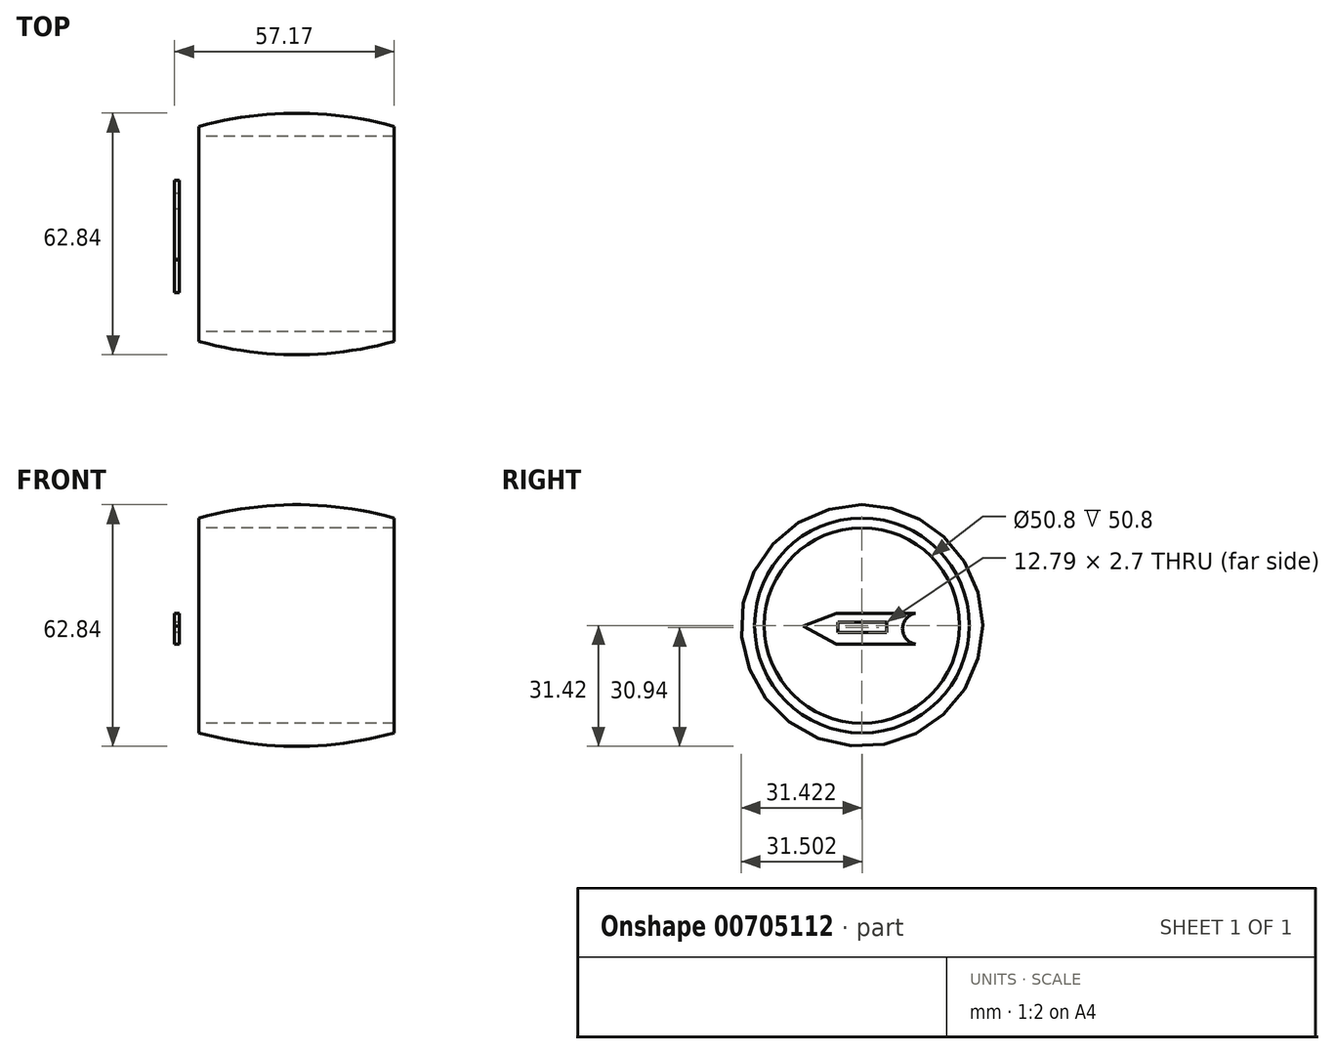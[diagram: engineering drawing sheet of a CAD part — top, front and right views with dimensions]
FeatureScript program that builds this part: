
annotation { "Feature Type Name" : "Feature", "Feature Type Description" : "" }
export const myFeature = defineFeature(function(context is Context, id is Id, definition is map)
    precondition{}
    {
        {
            var Q0;
            Q0=qCreatedBy(makeId("Right.planeOp"),FACE);
            var sketch = newSketch(context, id + "F0", { "sketchPlane" : qUnion([Q0])});
            skLineSegment(sketch, "E0", {"start": v(-101.6, -31.75) * mm, "end": v(153.5, -31.75) * mm, "construction": true});
            skCircle(sketch, "E1", {"center": v(-72.7, 0) * mm, "radius": 31.75 * mm});
            skCircle(sketch, "E2", {"center": v(130.5, -3.17) * mm, "radius": 28.58 * mm});
            skLineSegment(sketch, "E3", {"start": v(130.5, -3.18) * mm, "end": v(61.5, 57.58) * mm});
            skLineSegment(sketch, "E4", {"start": v(64.6, 54.85) * mm, "end": v(61.5, 51.33) * mm});
            skLineSegment(sketch, "E5", {"start": v(61.5, 51.33) * mm, "end": v(80.38, 34.69) * mm});
            skLineSegment(sketch, "E6", {"start": v(80.38, 34.69) * mm, "end": v(83.49, 38.21) * mm});
            skLineSegment(sketch, "E7", {"start": v(-72.7, 0) * mm, "end": v(65.82, 47.52) * mm});
            skLineSegment(sketch, "E8", {"start": v(-72.7, 0) * mm, "end": v(-14.9, -26.91) * mm});
            skLineSegment(sketch, "E9", {"start": v(-14.9, -26.91) * mm, "end": v(50.1, -26.91) * mm});
            skLineSegment(sketch, "E10", {"start": v(56.18, -22.36) * mm, "end": v(74.58, 39.8) * mm});
            skLineSegment(sketch, "E11", {"start": v(-14.9, -26.91) * mm, "end": v(-14.9, 19.83) * mm});
            skLineSegment(sketch, "E12", {"start": v(71.18, 28.32) * mm, "end": v(38.25, 38.06) * mm});
            skLineSegment(sketch, "E13", {"start": v(-58.83, 4.76) * mm, "end": v(-79.72, 4.76) * mm});
            skLineSegment(sketch, "E14", {"start": v(-58.83, -6.46) * mm, "end": v(-79.72, -6.46) * mm});
            skPoint(sketch, "E15.visualSharp", {"position": v(54.84, -26.91) * mm});
            skArc(sketch, "E15.filletArc", {"start": v(50.1, -26.91) * mm, "mid": v(53.9, -25.65) * mm, "end": v(56.18, -22.36) * mm});
            skCircle(sketch, "E16.0", {"center": v(-72.7, 0) * mm, "radius": 25.4 * mm});
            skCircle(sketch, "E17.0", {"center": v(130.5, -3.17) * mm, "radius": 22.23 * mm});
            skSolve(sketch);
        }
        {
            var Q0;
            Q0=qCreatedBy(makeId("Top.planeOp"),FACE);
            var Q1;
            Q1=sQuery(id+"F0.wireOp",VERTEX,"E8.start");
            cPlane(context, id + "F1", {"entities" : qUnion([Q0, Q1]), "cplaneType" : CPlaneType.PLANE_POINT, "offset" : 25.4 * mm, "width" : 152.4 * mm, "height" : 152.4 * mm});
        }
        {
            var Q0;
            Q0=qCreatedBy(id+"F1.planeOp",FACE);
            var sketch = newSketch(context, id + "F2", { "sketchPlane" : qUnion([Q0])});
            skLineSegment(sketch, "E18", {"start": v(0, -240.54) * mm, "end": v(0, 31.8) * mm, "construction": true});
            skLineSegment(sketch, "E19", {"start": v(-71.33, -156.1) * mm, "end": v(85.42, -156.1) * mm, "construction": true});
            skLineSegment(sketch, "E20", {"start": v(-25.4, -47.3) * mm, "end": v(25.4, -47.3) * mm});
            skPoint(sketch, "E21", {"position": v(0, -47.3) * mm});
            skLineSegment(sketch, "E22", {"start": v(25.4, -47.3) * mm, "end": v(25.4, -44.77) * mm});
            skLineSegment(sketch, "E23", {"start": v(-25.4, -47.3) * mm, "end": v(-25.4, -44.77) * mm});
            skArc(sketch, "E24", {"start": v(25.4, -44.77) * mm, "mid": v(0, -41.29) * mm, "end": v(-25.4, -44.77) * mm});
            skLineSegment(sketch, "E25", {"start": v(-23.52, -72.7) * mm, "end": v(23.66, -72.7) * mm, "construction": true});
            skSolve(sketch);
        }
        {
            var Q0;
            Q0=makeQuery(id+"F2.imprint","IMPRINT",FACE,{"disambiguationData":[TD([[makeQuery(id+"F2.imprint","IMPRINT",EDGE,{"derivedFrom":sQuery(id+"F2.wireOp",EDGE,"E20")}),1.0]])]});
            var Q1;
            Q1=sQuery(id+"F0.wireOp",EDGE,"E16.0");
            revolve(context, id + "F3", {"surfaceOperationType" : NewSurfaceOperationType.NEW, "entities" : qUnion([Q0]), "axis" : qUnion([Q1]), "revolveType" : RevolveType.FULL});
        }
        {
            var Q0;
            Q0=qCreatedBy(id+"F1.planeOp",FACE);
            var sketch = newSketch(context, id + "F4", { "sketchPlane" : qUnion([Q0])});
            skLineSegment(sketch, "E26", {"start": v(-28.81, -47.61) * mm, "end": v(-28.81, -41.26) * mm});
            skLineSegment(sketch, "E27", {"start": v(29.5, -47.42) * mm, "end": v(29.5, -41.07) * mm});
            skArc(sketch, "E28", {"start": v(29.5, -41.07) * mm, "mid": v(0.32, -36.16) * mm, "end": v(-28.81, -41.26) * mm});
            skSolve(sketch);
        }
        {
            var Q0;
            Q0=sQuery(id+"F4.wireOp",EDGE,"E26");
            var Q1;
            Q1=sQuery(id+"F4.wireOp",EDGE,"E28");
            var Q2;
            Q2=sQuery(id+"F4.wireOp",EDGE,"E27");
            var Q3;
            Q3=sQuery(id+"F0.wireOp",EDGE,"E16.0");
            revolve(context, id + "F5", {"bodyType" : ToolBodyType.SURFACE, "surfaceOperationType" : NewSurfaceOperationType.NEW, "surfaceEntities" : qUnion([Q0, Q1, Q2]), "axis" : qUnion([Q3]), "revolveType" : RevolveType.ONE_DIRECTION, "angle" : 130 * degree});
        }
        {
            var Q0;
            Q0=sQuery(id+"F0.wireOp",EDGE,"E7");
            cPlane(context, id + "F6", {"entities" : qUnion([Q0]), "cplaneType" : CPlaneType.LINE_ANGLE, "offset" : 25.4 * mm, "angle" : 0 * degree, "width" : 152.4 * mm, "height" : 152.4 * mm});
        }
        {
            var Q0;
            Q0=qCreatedBy(id+"F6.planeOp",FACE);
            var sketch = newSketch(context, id + "F7", { "sketchPlane" : qUnion([Q0])});
            skLineSegment(sketch, "E29", {"start": v(0, -0.48) * mm, "end": v(-31.13, -26.6) * mm});
            skLineSegment(sketch, "E30", {"start": v(0, -0.48) * mm, "end": v(31.13, -26.6) * mm});
            skLineSegment(sketch, "E31", {"start": v(-31.13, -26.6) * mm, "end": v(31.13, -26.6) * mm});
            skLineSegment(sketch, "E32", {"start": v(-30.35, -23.32) * mm, "end": v(32.35, -23.32) * mm});
            skSolve(sketch);
        }
        {
            var Q0;
            Q0=sQuery(id+"F7.wireOp",VERTEX,"E31.start");
            var Q1;
            Q1=sQuery(id+"F7.wireOp",EDGE,"E31");
            cPlane(context, id + "F8", {"entities" : qUnion([Q0, Q1]), "cplaneType" : CPlaneType.LINE_POINT, "offset" : 25.4 * mm, "width" : 152.4 * mm, "height" : 152.4 * mm});
        }
        {
            var Q0;
            Q0=qCreatedBy(id+"F8.planeOp",FACE);
            var sketch = newSketch(context, id + "F9", { "sketchPlane" : qUnion([Q0])});
            skLineSegment(sketch, "E33", {"start": v(-79.72, 4.76) * mm, "end": v(-91.78, 0) * mm});
            skLineSegment(sketch, "E34", {"start": v(-91.78, 0) * mm, "end": v(-79.72, -6.46) * mm});
            skLineSegment(sketch, "E35", {"start": v(-79.72, 4.76) * mm, "end": v(-58.93, 4.76) * mm});
            skLineSegment(sketch, "E36", {"start": v(-79.72, -6.46) * mm, "end": v(-59.06, -6.46) * mm});
            skLineSegment(sketch, "E37", {"start": v(-58.93, 4.76) * mm, "end": v(-32.82, 13.68) * mm});
            skLineSegment(sketch, "E38", {"start": v(-59.06, -6.46) * mm, "end": v(-15.42, -27.25) * mm});
            skSolve(sketch);
        }
        {
            var Q0;
            Q0=sQuery(id+"F7.wireOp",VERTEX,"E30.start");
            var Q1;
            Q1=sQuery(id+"F7.wireOp",EDGE,"E29");
            cPlane(context, id + "F10", {"entities" : qUnion([Q0, Q1]), "cplaneType" : CPlaneType.LINE_POINT, "offset" : 25.4 * mm, "width" : 152.4 * mm, "height" : 152.4 * mm});
        }
        {
            var Q0;
            Q0=qCreatedBy(id+"F10.planeOp",FACE);
            var sketch = newSketch(context, id + "F11", { "sketchPlane" : qUnion([Q0])});
            skCircle(sketch, "E39", {"center": v(9.98, 21.38) * mm, "radius": 1.59 * mm});
            skSolve(sketch);
        }
        {
            var Q0;
            Q0=makeQuery(id+"F5.opRevolve","SWEPT_EDGE",EDGE,{"disambiguationData":[OSD([sQuery(id+"F4.wireOp",VERTEX,"E28.end")])]});
            var Q1;
            Q1=makeQuery(id+"F5.opRevolve","SWEPT_EDGE",EDGE,{"disambiguationData":[OSD([sQuery(id+"F4.wireOp",VERTEX,"E27.end")])]});
            fillet(context, id + "F12", {"entities" : qUnion([Q0, Q1]), "radius" : 5.08 * mm, "tangentPropagation" : true, "allowEdgeOverflow" : false});
        }
        {
            var Q0;
            Q0=qCreatedBy(id+"F8.planeOp",FACE);
            var sketch = newSketch(context, id + "F13", { "sketchPlane" : qUnion([Q0])});
            skLineSegment(sketch, "E40", {"start": v(-87.98, -0.22) * mm, "end": v(-79.42, 3.18) * mm});
            skLineSegment(sketch, "E41", {"start": v(-87.98, -0.22) * mm, "end": v(-79.33, -4.86) * mm});
            skLineSegment(sketch, "E42", {"start": v(-79.33, -4.86) * mm, "end": v(-58.77, -4.86) * mm});
            skLineSegment(sketch, "E43", {"start": v(-79.42, 3.18) * mm, "end": v(-58.77, 3.18) * mm});
            skArc(sketch, "E44", {"start": v(-58.77, 3.18) * mm, "mid": v(-62.16, -0.84) * mm, "end": v(-58.77, -4.86) * mm});
            skLineSegment(sketch, "E45.bottom", {"start": v(-79.02, -1.83) * mm, "end": v(-66.24, -1.83) * mm});
            skLineSegment(sketch, "E45.top", {"start": v(-79.02, 0.87) * mm, "end": v(-66.24, 0.87) * mm});
            skLineSegment(sketch, "E45.left", {"start": v(-79.02, -1.83) * mm, "end": v(-79.02, 0.87) * mm});
            skLineSegment(sketch, "E45.right", {"start": v(-66.24, -1.83) * mm, "end": v(-66.24, 0.87) * mm});
            skPoint(sketch, "E45.middle", {"position": v(-72.63, -0.48) * mm});
            skSolve(sketch);
        }
        {
            var Q0;
            Q0=makeQuery(id+"F13.imprint","IMPRINT",FACE,{"disambiguationData":[TD([[makeQuery(id+"F13.imprint","IMPRINT",EDGE,{"derivedFrom":sQuery(id+"F13.wireOp",EDGE,"E40")}),-1.0]])]});
            extrude(context, id + "F14", {"entities" : qUnion([Q0]), "depth" : 0.64 * mm, "offsetDistance" : 25.4 * mm, "hasSecondDirection" : true, "secondDirectionOppositeDirection" : true, "secondDirectionDepth" : 0.64 * mm});
        }
    });
